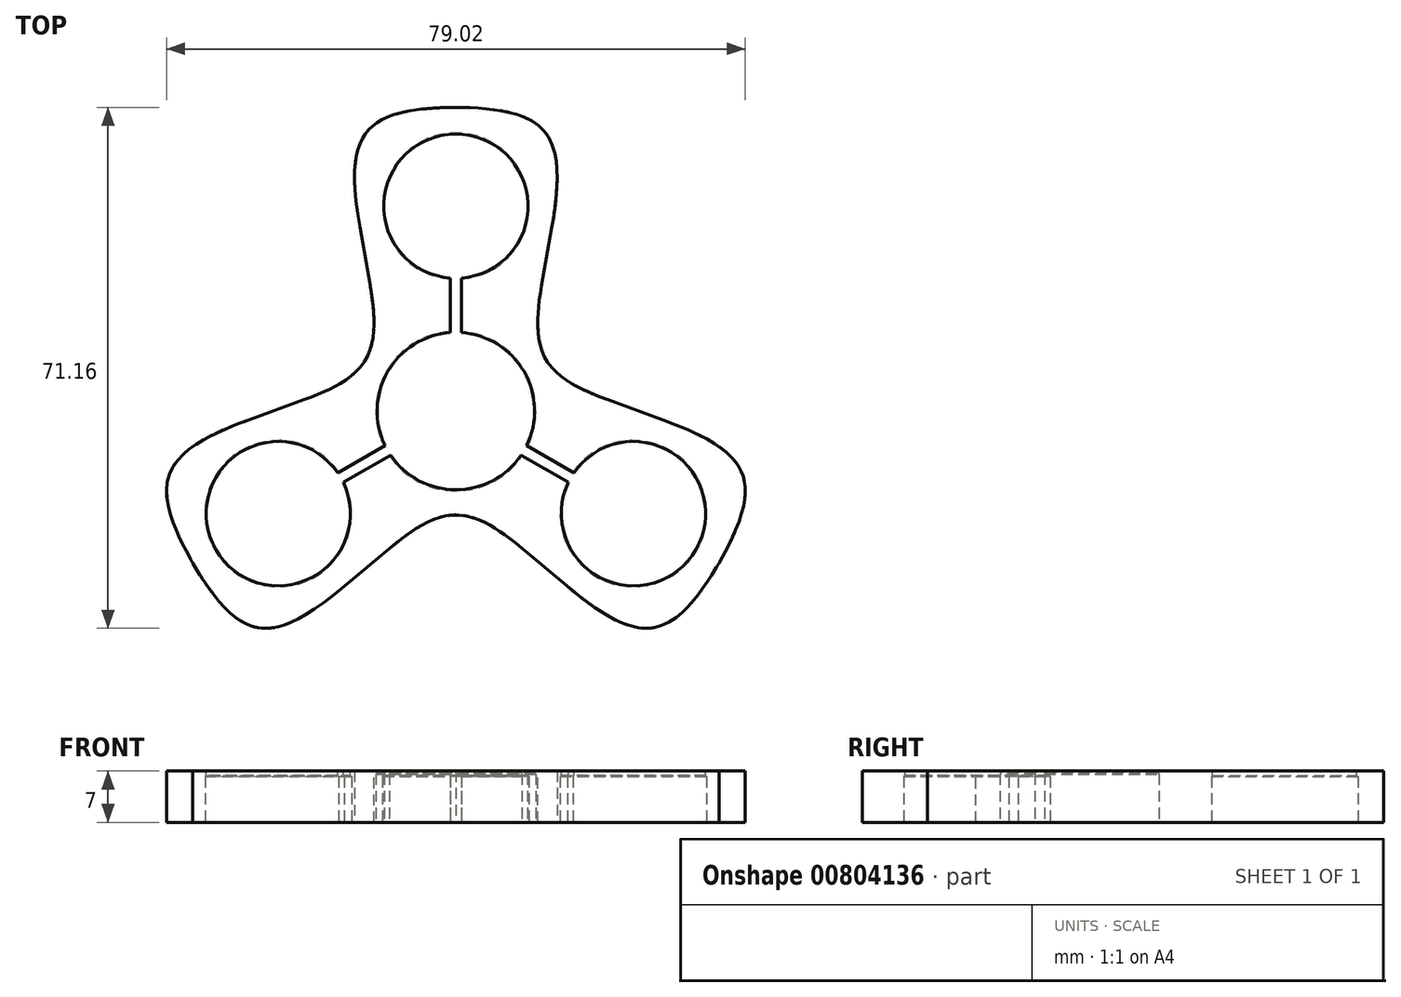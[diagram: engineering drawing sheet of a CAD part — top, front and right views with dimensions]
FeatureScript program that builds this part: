
annotation { "Feature Type Name" : "Feature", "Feature Type Description" : "" }
export const myFeature = defineFeature(function(context is Context, id is Id, definition is map)
    precondition{}
    {
        {
            var Q0;
            Q0=qCreatedBy(makeId("Top.planeOp"),FACE);
            var sketch = newSketch(context, id + "F0", { "sketchPlane" : qUnion([Q0])});
            skLineSegment(sketch, "E0", {"start": v(0, 0) * mm, "end": v(71.88, 41.5) * mm, "construction": true});
            skLineSegment(sketch, "E1", {"start": v(0, 0) * mm, "end": v(-71.88, 41.5) * mm, "construction": true});
            skCircle(sketch, "E2", {"center": v(0, 0) * mm, "radius": 10.9 * mm, "construction": true});
            skCircle(sketch, "E3", {"center": v(0, 28) * mm, "radius": 10 * mm});
            skLineSegment(sketch, "E4", {"start": v(-16, 41.5) * mm, "end": v(16, 41.5) * mm});
            skLineSegment(sketch, "E5", {"start": v(16, 41.5) * mm, "end": v(9.67, 5.58) * mm});
            skLineSegment(sketch, "E6", {"start": v(-16, 41.5) * mm, "end": v(-9.67, 5.58) * mm});
            skLineSegment(sketch, "E7", {"start": v(0, 28) * mm, "end": v(0, 41.5) * mm, "construction": true});
            skPoint(sketch, "E8", {"position": v(0, 38) * mm});
            skArc(sketch, "E9", {"start": v(9.44, 5.45) * mm, "mid": v(0, 10.9) * mm, "end": v(-9.44, 5.45) * mm});
            skLineSegment(sketch, "E10", {"start": v(-9.44, 5.45) * mm, "end": v(-9.67, 5.58) * mm});
            skLineSegment(sketch, "E11", {"start": v(9.44, 5.45) * mm, "end": v(9.67, 5.58) * mm});
            skSolve(sketch);
        }
        {
            assignVariable(context, id + "F1", {"name" : "ledge", "anyValue" : 0.15});
        }
        {
            var Q0;
            Q0=qSketchRegion(id+"F0",true);
            extrude(context, id + "F2", {"entities" : qUnion([Q0]), "endBound" : BoundingType.SYMMETRIC, "depth" : 7 * mm, "offsetDistance" : 25 * mm});
        }
        {
            var Q0;
            Q0=makeQuery(id+"F2.opExtrude","SWEPT_EDGE",EDGE,{"disambiguationData":[OSD([sQuery(id+"F0.wireOp",EDGE,"E4"),sQuery(id+"F0.wireOp",EDGE,"E6")])]});
            var Q1;
            Q1=makeQuery(id+"F2.opExtrude","SWEPT_EDGE",EDGE,{"disambiguationData":[OSD([sQuery(id+"F0.wireOp",EDGE,"E4"),sQuery(id+"F0.wireOp",EDGE,"E5")])]});
            fillet(context, id + "F3", {"entities" : qUnion([Q0, Q1]), "radius" : 14 * mm, "tangentPropagation" : true, "rho" : .6, "crossSection" : FilletCrossSection.CONIC, "allowEdgeOverflow" : false});
        }
        {
            var Q0;
            Q0=makeQuery(id+"F2.opExtrude","CAP_FACE",FACE,{"disambiguationData":[OSD([sQuery(id+"F0.wireOp",EDGE,"E3"),sQuery(id+"F0.wireOp",EDGE,"E4"),sQuery(id+"F0.wireOp",EDGE,"E5"),sQuery(id+"F0.wireOp",EDGE,"E6"),sQuery(id+"F0.wireOp",EDGE,"E9"),sQuery(id+"F0.wireOp",EDGE,"E10"),sQuery(id+"F0.wireOp",EDGE,"E11")])],"isStart":false});
            var sketch = newSketch(context, id + "F4", { "sketchPlane" : qUnion([Q0])});
            skCircle(sketch, "E12.0", {"center": v(0, 28) * mm, "radius": 10 * mm});
            skCircle(sketch, "E13.0", {"center": v(0, 28) * mm, "radius": 9.85 * mm});
            skArc(sketch, "E14.0", {"start": v(9.44, 5.45) * mm, "mid": v(0, 10.9) * mm, "end": v(-9.44, 5.45) * mm});
            skArc(sketch, "E15.0", {"start": v(9.3, 5.37) * mm, "mid": v(0, 10.75) * mm, "end": v(-9.3, 5.37) * mm});
            skLineSegment(sketch, "E16", {"start": v(-9.3, 5.37) * mm, "end": v(-9.44, 5.45) * mm});
            skLineSegment(sketch, "E17", {"start": v(9.3, 5.37) * mm, "end": v(9.44, 5.45) * mm});
            skSolve(sketch);
        }
        {
            var Q0;
            Q0=makeQuery(id+"F4.imprint","IMPRINT",FACE,{"disambiguationData":[TD([[makeQuery(id+"F4.imprint","IMPRINT",EDGE,{"derivedFrom":sQuery(id+"F4.wireOp",EDGE,"E12.0")}),1.0]])]});
            extrude(context, id + "F5", {"entities" : qUnion([Q0]), "operationType" : NewBodyOperationType.ADD, "oppositeDirection" : true, "depth" : .75 * mm, "offsetDistance" : 25 * mm});
        }
        {
            var Q0;
            Q0=makeQuery(id+"F4.imprint","IMPRINT",FACE,{"disambiguationData":[TD([[makeQuery(id+"F4.imprint","IMPRINT",EDGE,{"derivedFrom":sQuery(id+"F4.wireOp",EDGE,"E14.0")}),1.0]])]});
            extrude(context, id + "F6", {"entities" : qUnion([Q0]), "operationType" : NewBodyOperationType.ADD, "oppositeDirection" : true, "depth" : .4 * mm, "offsetDistance" : 25 * mm});
        }
        {
            var Q0;
            Q0=makeQuery(id+"F5.opExtrude","CAP_EDGE",EDGE,{"disambiguationData":[OSD([sQuery(id+"F4.wireOp",EDGE,"E13.0")])],"isStart":false});
            var Q1;
            Q1=makeQuery(id+"F6.opExtrude","CAP_EDGE",EDGE,{"disambiguationData":[OSD([sQuery(id+"F4.wireOp",EDGE,"E15.0")])],"isStart":false});
            chamfer(context, id + "F7", {"entities" : qUnion([Q0, Q1]), "width" : (getVariable(context, 'ledge')) * mm, "tangentPropagation" : true});
        }
        {
            var Q0;
            Q0=qCreatedBy(makeId("Top.planeOp"),FACE);
            var sketch = newSketch(context, id + "F8", { "sketchPlane" : qUnion([Q0])});
            skLineSegment(sketch, "E18.bottom", {"start": v(-0.75, 0) * mm, "end": v(0.75, 0) * mm});
            skLineSegment(sketch, "E18.top", {"start": v(-0.75, 28) * mm, "end": v(0.75, 28) * mm});
            skLineSegment(sketch, "E18.left", {"start": v(-0.75, 0) * mm, "end": v(-0.75, 28) * mm});
            skLineSegment(sketch, "E18.right", {"start": v(0.75, 0) * mm, "end": v(0.75, 28) * mm});
            skPoint(sketch, "E19", {"position": v(0, 28) * mm});
            skSolve(sketch);
        }
        {
            var Q0;
            Q0=makeQuery(id+"F8.imprint","IMPRINT",FACE,{"disambiguationData":[TD([[makeQuery(id+"F8.imprint","IMPRINT",EDGE,{"derivedFrom":sQuery(id+"F8.wireOp",EDGE,"E18.bottom")}),1.0]])]});
            extrude(context, id + "F9", {"entities" : qUnion([Q0]), "operationType" : NewBodyOperationType.REMOVE, "endBound" : BoundingType.THROUGH_ALL, "depth" : 25 * mm, "offsetDistance" : 25 * mm, "hasSecondDirection" : true, "secondDirectionBound" : SecondDirectionBoundingType.THROUGH_ALL, "secondDirectionOppositeDirection" : true, "secondDirectionDepth" : 25 * mm});
        }
        {
            var Q0;
            Q0=qCreatedBy(makeId("Front.planeOp"),FACE);
            var sketch = newSketch(context, id + "F10", { "sketchPlane" : qUnion([Q0])});
            skLineSegment(sketch, "E20", {"start": v(0, 0) * mm, "end": v(0, 20.55) * mm, "construction": true});
            skSolve(sketch);
        }
        {
            var Q0;
            Q0=makeQuery(id+"F2.opExtrude","SWEPT_BODY",BODY,{"disambiguationData":[OSD([sQuery(id+"F0.wireOp",EDGE,"E3"),sQuery(id+"F0.wireOp",EDGE,"E4"),sQuery(id+"F0.wireOp",EDGE,"E5"),sQuery(id+"F0.wireOp",EDGE,"E6"),sQuery(id+"F0.wireOp",EDGE,"E9"),sQuery(id+"F0.wireOp",EDGE,"E10"),sQuery(id+"F0.wireOp",EDGE,"E11")])]});
            var Q1;
            Q1=sQuery(id+"F10.wireOp",EDGE,"E20");
            circularPattern(context, id + "F11", {"operationType" : NewBodyOperationType.ADD, "entities" : qUnion([Q0]), "axis" : qUnion([Q1]), "angle" : 360 * degree, "instanceCount" : 3, "equalSpace" : true});
        }
        {
            var Q0;
            Q0=makeQuery(id+"F11.boolean.opBoolean","MERGE",EDGE,{"derivedFrom":[makeQuery(id+"F2.opExtrude","SWEPT_EDGE",EDGE,{"disambiguationData":[OSD([sQuery(id+"F0.wireOp",EDGE,"E5"),sQuery(id+"F0.wireOp",EDGE,"E11")])]}),makeQuery(id+"F11.opPattern","COPY",EDGE,{"derivedFrom":makeQuery(id+"F2.opExtrude","SWEPT_EDGE",EDGE,{"disambiguationData":[OSD([sQuery(id+"F0.wireOp",EDGE,"E6"),sQuery(id+"F0.wireOp",EDGE,"E10")])]}),"instanceName":"2"})]});
            var Q1;
            Q1=makeQuery(id+"F11.boolean.opBoolean","MERGE",EDGE,{"derivedFrom":[makeQuery(id+"F2.opExtrude","SWEPT_EDGE",EDGE,{"disambiguationData":[OSD([sQuery(id+"F0.wireOp",EDGE,"E6"),sQuery(id+"F0.wireOp",EDGE,"E10")])]}),makeQuery(id+"F11.opPattern","COPY",EDGE,{"derivedFrom":makeQuery(id+"F2.opExtrude","SWEPT_EDGE",EDGE,{"disambiguationData":[OSD([sQuery(id+"F0.wireOp",EDGE,"E5"),sQuery(id+"F0.wireOp",EDGE,"E11")])]}),"instanceName":"1"})]});
            var Q2;
            Q2=makeQuery(id+"F11.boolean.opBoolean","MERGE",EDGE,{"derivedFrom":[makeQuery(id+"F11.opPattern","COPY",EDGE,{"derivedFrom":makeQuery(id+"F2.opExtrude","SWEPT_EDGE",EDGE,{"disambiguationData":[OSD([sQuery(id+"F0.wireOp",EDGE,"E6"),sQuery(id+"F0.wireOp",EDGE,"E10")])]}),"instanceName":"1"}),makeQuery(id+"F11.opPattern","COPY",EDGE,{"derivedFrom":makeQuery(id+"F2.opExtrude","SWEPT_EDGE",EDGE,{"disambiguationData":[OSD([sQuery(id+"F0.wireOp",EDGE,"E5"),sQuery(id+"F0.wireOp",EDGE,"E11")])]}),"instanceName":"2"})]});
            fillet(context, id + "F12", {"entities" : qUnion([Q0, Q1, Q2]), "radius" : 14 * mm, "tangentPropagation" : true, "rho" : .6, "crossSection" : FilletCrossSection.CONIC, "allowEdgeOverflow" : false});
        }
    });
